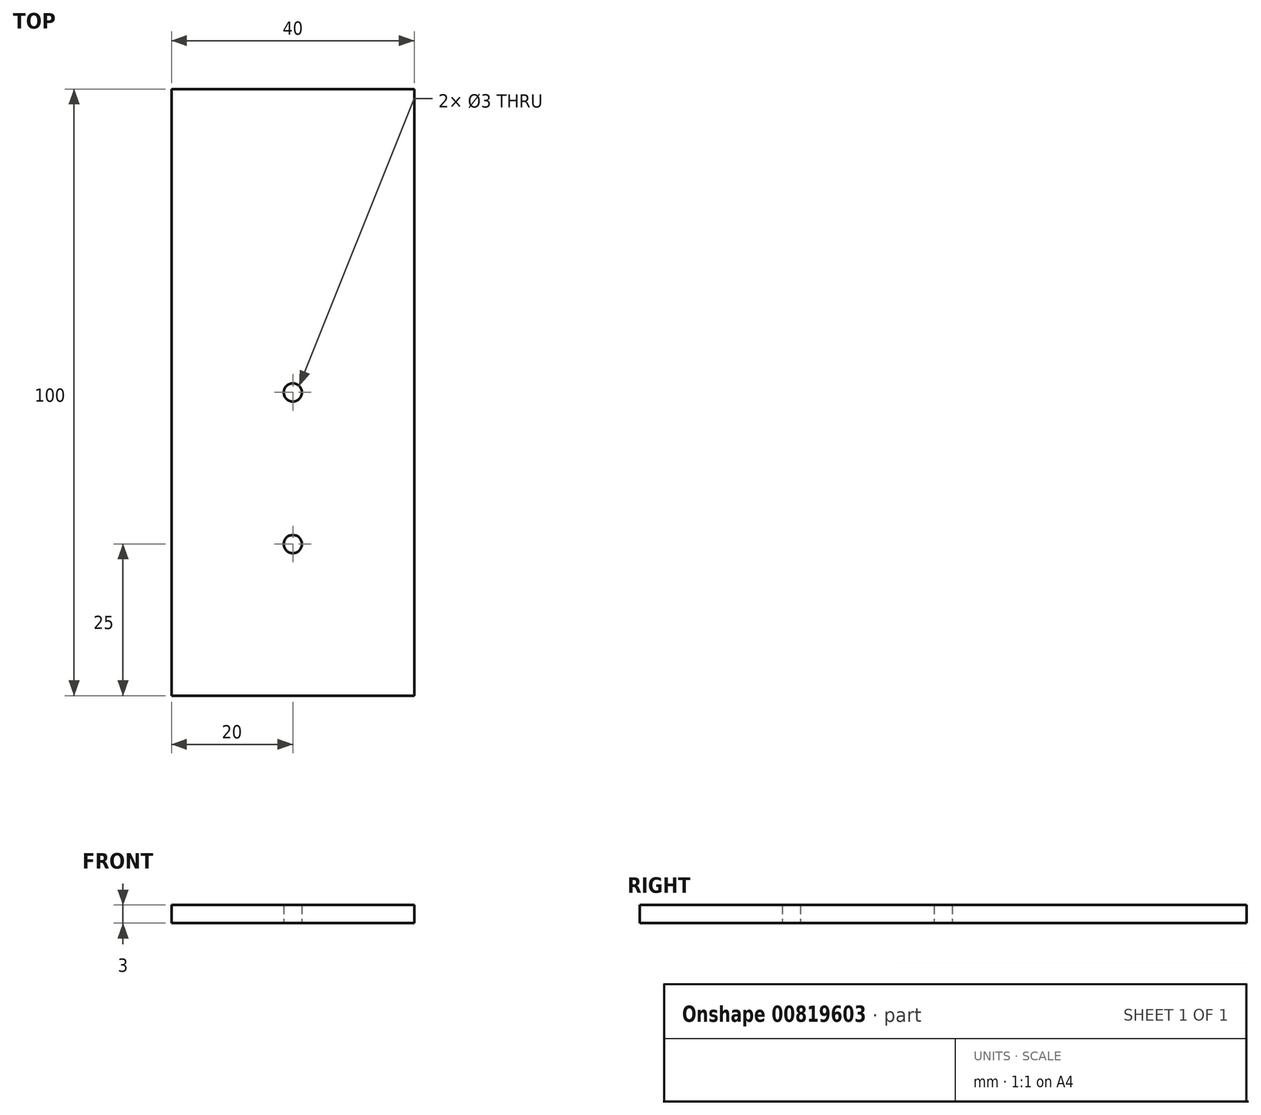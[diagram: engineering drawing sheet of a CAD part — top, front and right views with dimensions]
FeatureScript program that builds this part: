
annotation { "Feature Type Name" : "Feature", "Feature Type Description" : "" }
export const myFeature = defineFeature(function(context is Context, id is Id, definition is map)
    precondition{}
    {
        {
            var Q0;
            Q0=qCreatedBy(makeId("Top.planeOp"),FACE);
            var sketch = newSketch(context, id + "F0", { "sketchPlane" : qUnion([Q0])});
            skLineSegment(sketch, "E0.bottom", {"start": v(0, 0) * mm, "end": v(-40, 0) * mm});
            skLineSegment(sketch, "E0.top", {"start": v(0, 100) * mm, "end": v(-40, 100) * mm});
            skLineSegment(sketch, "E0.left", {"start": v(0, 0) * mm, "end": v(0, 100) * mm});
            skLineSegment(sketch, "E0.right", {"start": v(-40, 0) * mm, "end": v(-40, 100) * mm});
            skSolve(sketch);
        }
        {
            var Q0;
            Q0 = qSketchRegion(id + "F0", true);
            extrude(context, id + "F1", {"entities" : qUnion([Q0]), "depth" : 3 * mm, "offsetDistance" : 25 * mm});
        }
        {
            var Q0;
            Q0=qCreatedBy(makeId("Top.planeOp"),FACE);
            var sketch = newSketch(context, id + "F2", { "sketchPlane" : qUnion([Q0])});
            skLineSegment(sketch, "E1", {"start": v(-20, 25) * mm, "end": v(-20, 50) * mm});
            skSolve(sketch);
        }
        {
            var Q0;
            Q0=sQuery(id+"F2.wireOp",VERTEX,"E1.end");
            var Q1;
            Q1=sQuery(id+"F2.wireOp",VERTEX,"E1.start");
            var Q2;
            Q2=makeQuery(id+"F1.opExtrude","SWEPT_BODY",BODY,{"disambiguationData":[OSD([sQuery(id+"F0.wireOp",EDGE,"E0.bottom"),sQuery(id+"F0.wireOp",EDGE,"E0.top"),sQuery(id+"F0.wireOp",EDGE,"E0.left"),sQuery(id+"F0.wireOp",EDGE,"E0.right")])]});
            hole(context, id + "F3", {"style" : HoleStyle.SIMPLE, "endStyle" : HoleEndStyle.THROUGH, "oppositeDirection" : true, "holeDiameter" : 3 * mm, "majorDiameter" : 5 * mm, "isTappedThrough" : true, "tappedDepth" : 12 * mm, "tapClearance" : 3, "locations" : qUnion([Q0, Q1]), "scope" : qUnion([Q2])});
        }
    });
